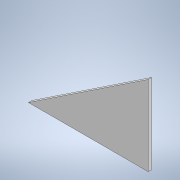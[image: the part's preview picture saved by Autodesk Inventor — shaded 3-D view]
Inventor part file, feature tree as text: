
AUTODESK INVENTOR PART (.ipt)
format: ipt  version: 2020.2 (Build 242310000, 310)  size: 89,600 bytes
history: native  units: in
note: dims shown in document units (in); Inventor stores cm internally (conversion verified against a paired STEP export)
features: extrude x1, sketch x1
ambient origin geometry x8: Origin, YZ Plane, XZ Plane, XY Plane, X Axis, Y Axis, Z Axis, Center Point
bodies: Solid1 (feature_tree)
feature tree (2):
  extrude  "Extrusion1"  Depth=1.0in
  sketch  "Sketch2"  dims[d2=36.0in d3=24.0in d4=1.0in d5=0.0in]
